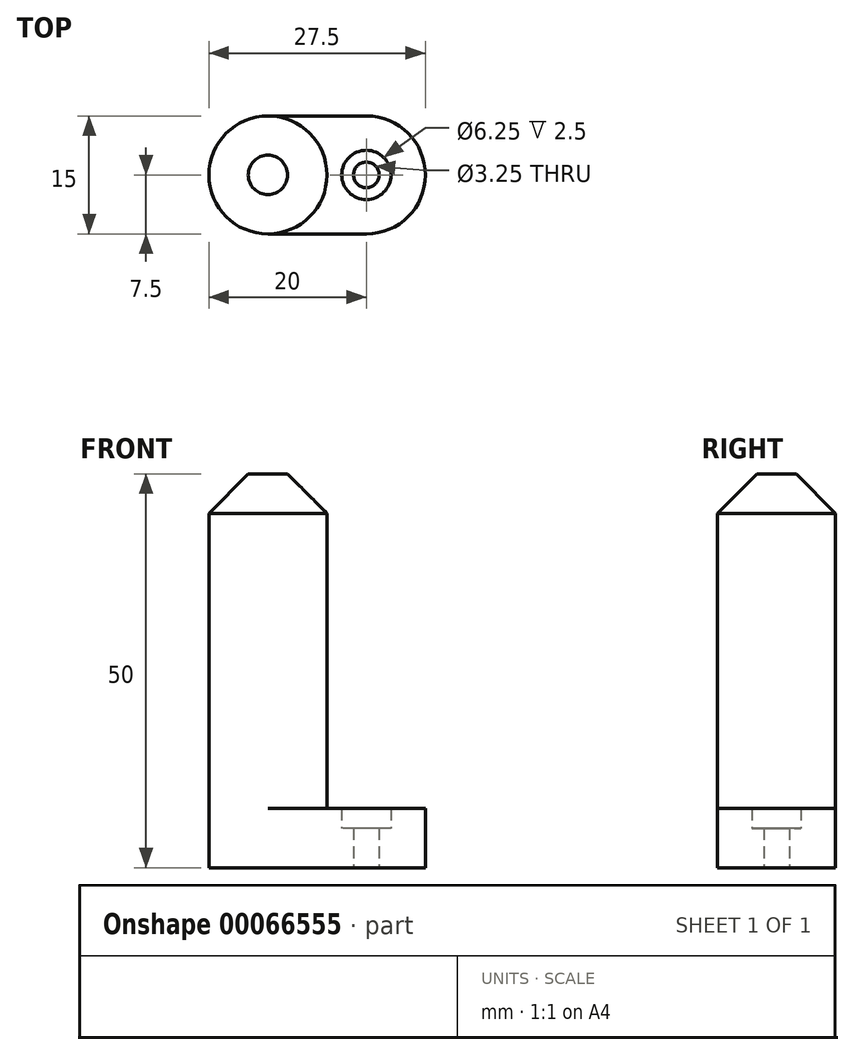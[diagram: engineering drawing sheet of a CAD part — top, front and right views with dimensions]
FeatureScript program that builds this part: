
annotation { "Feature Type Name" : "Feature", "Feature Type Description" : "" }
export const myFeature = defineFeature(function(context is Context, id is Id, definition is map)
    precondition{}
    {
        {
            var Q0;
            Q0=qCreatedBy(makeId("Top.planeOp"),FACE);
            var sketch = newSketch(context, id + "F0", { "sketchPlane" : qUnion([Q0])});
            skCircle(sketch, "E0", {"center": v(0, 0) * mm, "radius": 7.5 * mm});
            skLineSegment(sketch, "E1.bottom", {"start": v(0, 7.5) * mm, "end": v(12.5, 7.5) * mm});
            skLineSegment(sketch, "E1.top", {"start": v(0, -7.5) * mm, "end": v(12.5, -7.5) * mm});
            skLineSegment(sketch, "E1.right", {"start": v(20, 0) * mm, "end": v(20, 0) * mm});
            skPoint(sketch, "E2.visualSharp", {"position": v(20, 7.5) * mm});
            skArc(sketch, "E2.filletArc", {"start": v(20, 0) * mm, "mid": v(17.8, 5.3) * mm, "end": v(12.5, 7.5) * mm});
            skPoint(sketch, "E3.visualSharp", {"position": v(20, -7.5) * mm});
            skArc(sketch, "E3.filletArc", {"start": v(12.5, -7.5) * mm, "mid": v(17.8, -5.3) * mm, "end": v(20, 0) * mm});
            skCircle(sketch, "E4", {"center": v(12.5, 0) * mm, "radius": 1.63 * mm});
            skCircle(sketch, "E5", {"center": v(12.5, 0) * mm, "radius": 3.12 * mm});
            skSolve(sketch);
        }
        {
            var Q0;
            {var subQ0=sQuery(id+"F0.wireOp",EDGE,"E0");var subQ1=makeQuery(id+"F0.imprint","INTERSECT",VERTEX,{"derivedFrom":[subQ0,sQuery(id+"F0.wireOp",EDGE,"E1.bottom")]});Q0=makeQuery(id+"F0.imprint","IMPRINT",FACE,{"disambiguationData":[TD([[makeQuery(id+"F0.imprint","IMPRINT",EDGE,{"disambiguationData":[TD([[subQ1,-1.0]])],"derivedFrom":subQ0}),1.0]])]});}
            extrude(context, id + "F1", {"entities" : qUnion([Q0]), "depth" : 50 * mm});
        }
        {
            var Q0;
            {var subQ1=sQuery(id+"F0.wireOp",EDGE,"E1.bottom");Q0=makeQuery(id+"F0.imprint","IMPRINT",FACE,{"disambiguationData":[TD([[makeQuery(id+"F0.imprint","IMPRINT",EDGE,{"derivedFrom":subQ1}),-1.0]])]});}
            extrude(context, id + "F2", {"entities" : qUnion([Q0]), "operationType" : NewBodyOperationType.ADD, "depth" : 7.5 * mm});
        }
        {
            var Q0;
            Q0=makeQuery(id+"F0.imprint","IMPRINT",FACE,{"disambiguationData":[TD([[makeQuery(id+"F0.imprint","IMPRINT",EDGE,{"derivedFrom":sQuery(id+"F0.wireOp",EDGE,"E4")}),-1.0]])]});
            extrude(context, id + "F3", {"entities" : qUnion([Q0]), "operationType" : NewBodyOperationType.ADD, "depth" : 5 * mm});
        }
        {
            var Q0;
            Q0=makeQuery(id+"F1.opExtrude","CAP_EDGE",EDGE,{"disambiguationData":[OSD([sQuery(id+"F0.wireOp",EDGE,"E0")])],"isStart":false});
            chamfer(context, id + "F4", {"entities" : qUnion([Q0]), "width" : 5 * mm, "tangentPropagation" : true});
        }
    });
